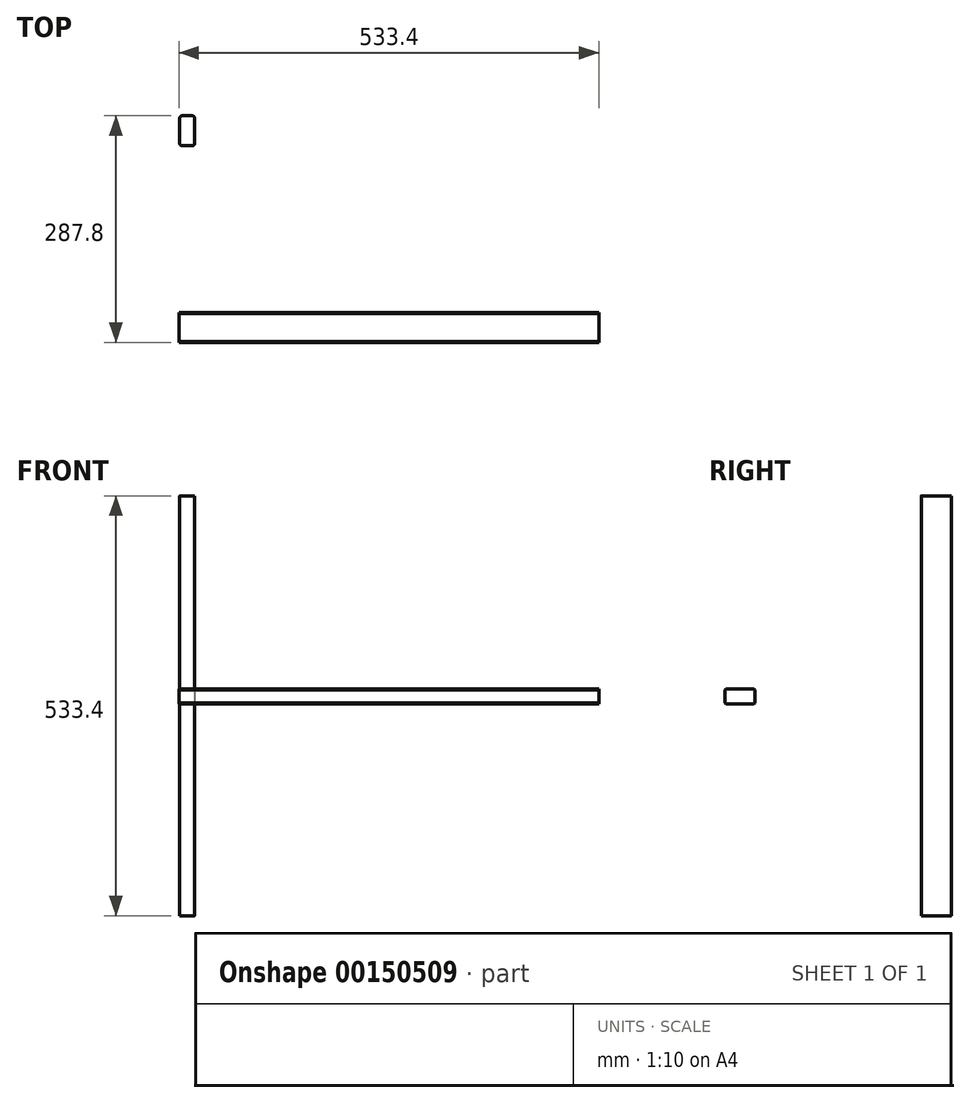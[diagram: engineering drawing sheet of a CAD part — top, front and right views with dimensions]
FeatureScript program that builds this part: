
annotation { "Feature Type Name" : "Feature", "Feature Type Description" : "" }
export const myFeature = defineFeature(function(context is Context, id is Id, definition is map)
    precondition{}
    {
        {
            var Q0;
            Q0=qCreatedBy(makeId("Right.planeOp"),FACE);
            var sketch = newSketch(context, id + "F0", { "sketchPlane" : qUnion([Q0])});
            skLineSegment(sketch, "E0.bottom", {"start": v(-53.15, 264.45) * mm, "end": v(-15.05, 264.45) * mm});
            skLineSegment(sketch, "E0.top", {"start": v(-53.15, -268.95) * mm, "end": v(-15.05, -268.95) * mm});
            skLineSegment(sketch, "E0.left", {"start": v(-53.15, 264.45) * mm, "end": v(-53.15, -268.95) * mm});
            skLineSegment(sketch, "E0.right", {"start": v(-15.05, 264.45) * mm, "end": v(-15.05, -268.95) * mm});
            skSolve(sketch);
        }
        {
            var Q0;
            Q0=makeQuery(id+"F0.imprint","IMPRINT",FACE,{"disambiguationData":[TD([[makeQuery(id+"F0.imprint","IMPRINT",EDGE,{"derivedFrom":sQuery(id+"F0.wireOp",EDGE,"E0.bottom")}),-1.0]])]});
            extrude(context, id + "F1", {"entities" : qUnion([Q0]), "depth" : 19.05 * mm});
        }
        {
            var Q0;
            Q0=makeQuery(id+"F1.opExtrude","CAP_EDGE",EDGE,{"disambiguationData":[OSD([sQuery(id+"F0.wireOp",EDGE,"E0.left")])],"isStart":true});
            var Q1;
            Q1=makeQuery(id+"F1.opExtrude","CAP_EDGE",EDGE,{"disambiguationData":[OSD([sQuery(id+"F0.wireOp",EDGE,"E0.left")])],"isStart":false});
            var Q2;
            Q2=makeQuery(id+"F1.opExtrude","CAP_EDGE",EDGE,{"disambiguationData":[OSD([sQuery(id+"F0.wireOp",EDGE,"E0.right")])],"isStart":true});
            var Q3;
            Q3=makeQuery(id+"F1.opExtrude","CAP_EDGE",EDGE,{"disambiguationData":[OSD([sQuery(id+"F0.wireOp",EDGE,"E0.right")])],"isStart":false});
            fillet(context, id + "F2", {"entities" : qUnion([Q0, Q1, Q2, Q3]), "radius" : 3.17 * mm, "tangentPropagation" : true, "allowEdgeOverflow" : false});
        }
        {
            var Q0;
            Q0=qCreatedBy(makeId("Top.planeOp"),FACE);
            var sketch = newSketch(context, id + "F3", { "sketchPlane" : qUnion([Q0])});
            skLineSegment(sketch, "E1.bottom", {"start": v(-0.97, -264.75) * mm, "end": v(532.43, -264.75) * mm});
            skLineSegment(sketch, "E1.top", {"start": v(-0.97, -302.85) * mm, "end": v(532.43, -302.85) * mm});
            skLineSegment(sketch, "E1.left", {"start": v(-0.97, -264.75) * mm, "end": v(-0.97, -302.85) * mm});
            skLineSegment(sketch, "E1.right", {"start": v(532.43, -264.75) * mm, "end": v(532.43, -302.85) * mm});
            skSolve(sketch);
        }
        {
            var Q0;
            Q0=makeQuery(id+"F3.imprint","IMPRINT",FACE,{"disambiguationData":[TD([[makeQuery(id+"F3.imprint","IMPRINT",EDGE,{"derivedFrom":sQuery(id+"F3.wireOp",EDGE,"E1.bottom")}),-1.0]])]});
            extrude(context, id + "F4", {"entities" : qUnion([Q0]), "depth" : 19.05 * mm});
        }
        {
            var Q0;
            Q0=makeQuery(id+"F4.opExtrude","CAP_EDGE",EDGE,{"disambiguationData":[OSD([sQuery(id+"F3.wireOp",EDGE,"E1.bottom")])],"isStart":true});
            var Q1;
            Q1=makeQuery(id+"F4.opExtrude","CAP_EDGE",EDGE,{"disambiguationData":[OSD([sQuery(id+"F3.wireOp",EDGE,"E1.bottom")])],"isStart":false});
            var Q2;
            Q2=makeQuery(id+"F4.opExtrude","CAP_EDGE",EDGE,{"disambiguationData":[OSD([sQuery(id+"F3.wireOp",EDGE,"E1.top")])],"isStart":true});
            var Q3;
            Q3=makeQuery(id+"F4.opExtrude","CAP_EDGE",EDGE,{"disambiguationData":[OSD([sQuery(id+"F3.wireOp",EDGE,"E1.top")])],"isStart":false});
            chamfer(context, id + "F5", {"entities" : qUnion([Q0, Q1, Q2, Q3]), "width" : 1.27 * mm, "tangentPropagation" : true});
        }
    });
